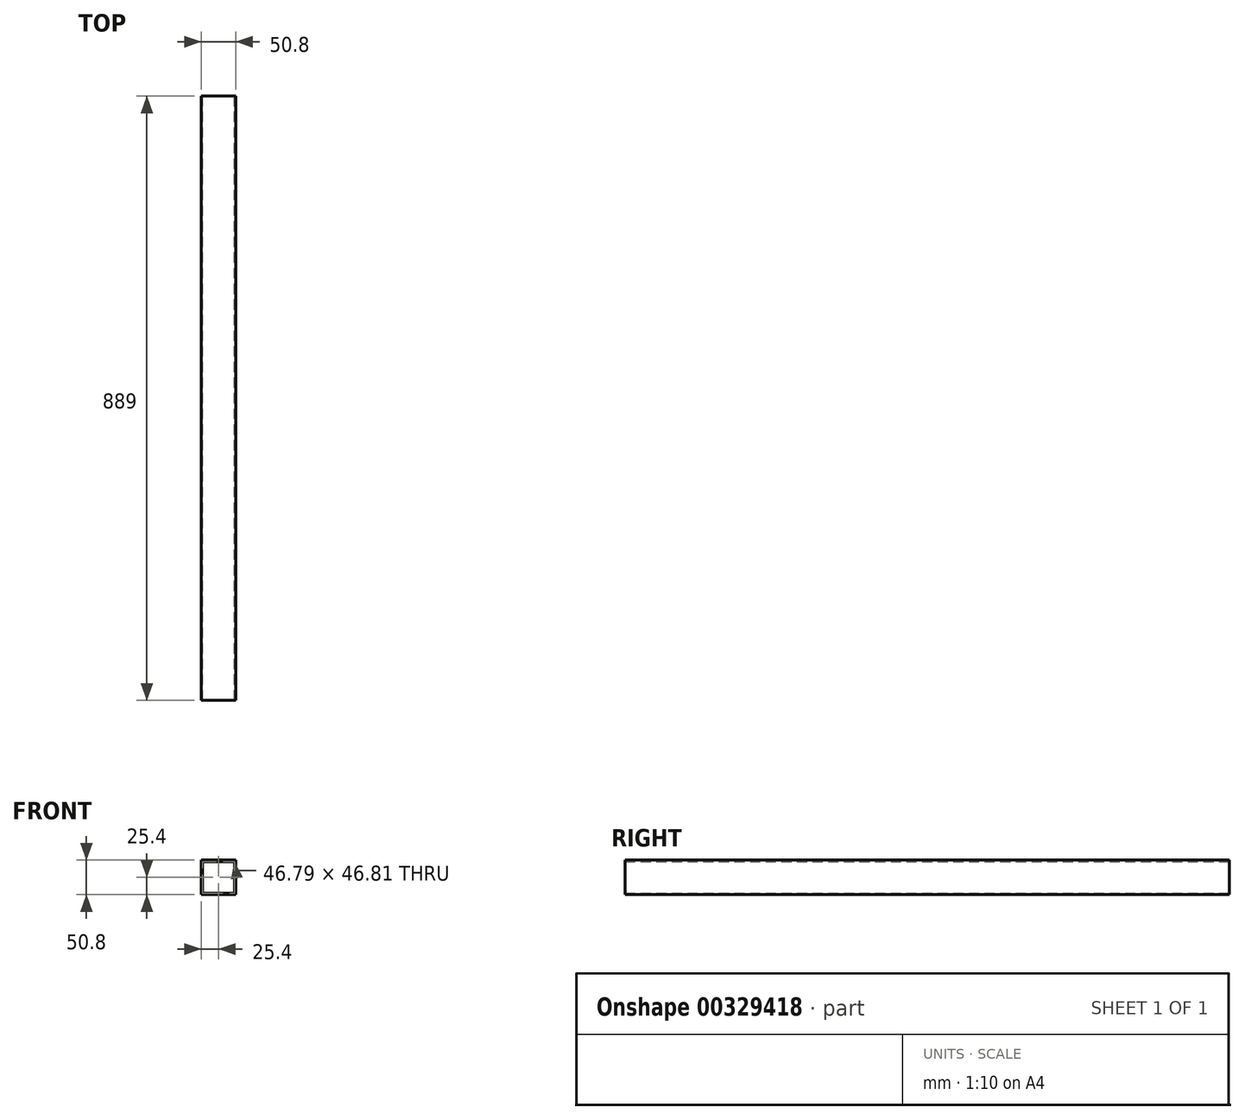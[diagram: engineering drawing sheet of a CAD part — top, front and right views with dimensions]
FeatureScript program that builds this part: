
annotation { "Feature Type Name" : "Feature", "Feature Type Description" : "" }
export const myFeature = defineFeature(function(context is Context, id is Id, definition is map)
    precondition{}
    {
        {
            var Q0;
            Q0=qCreatedBy(makeId("Front.planeOp"),FACE);
            var sketch = newSketch(context, id + "F0", { "sketchPlane" : qUnion([Q0])});
            skLineSegment(sketch, "E0.bottom", {"start": v(25.4, -25.4) * mm, "end": v(-25.4, -25.4) * mm});
            skLineSegment(sketch, "E0.top", {"start": v(25.4, 25.4) * mm, "end": v(-25.4, 25.4) * mm});
            skLineSegment(sketch, "E0.left", {"start": v(25.4, -25.4) * mm, "end": v(25.4, 25.4) * mm});
            skLineSegment(sketch, "E0.right", {"start": v(-25.4, -25.4) * mm, "end": v(-25.4, 25.4) * mm});
            skPoint(sketch, "E0.middle", {"position": v(0, 0) * mm});
            skLineSegment(sketch, "E1.bottom", {"start": v(23.4, -23.4) * mm, "end": v(-23.4, -23.4) * mm});
            skLineSegment(sketch, "E1.top", {"start": v(23.4, 23.4) * mm, "end": v(-23.4, 23.4) * mm});
            skLineSegment(sketch, "E1.left", {"start": v(23.4, -23.4) * mm, "end": v(23.4, 23.4) * mm});
            skLineSegment(sketch, "E1.right", {"start": v(-23.4, -23.4) * mm, "end": v(-23.4, 23.4) * mm});
            skSolve(sketch);
        }
        {
            var Q0;
            Q0=qSketchRegion(id+"F0",true);
            extrude(context, id + "F1", {"entities" : qUnion([Q0]), "depth" : 889 * mm});
        }
    });
